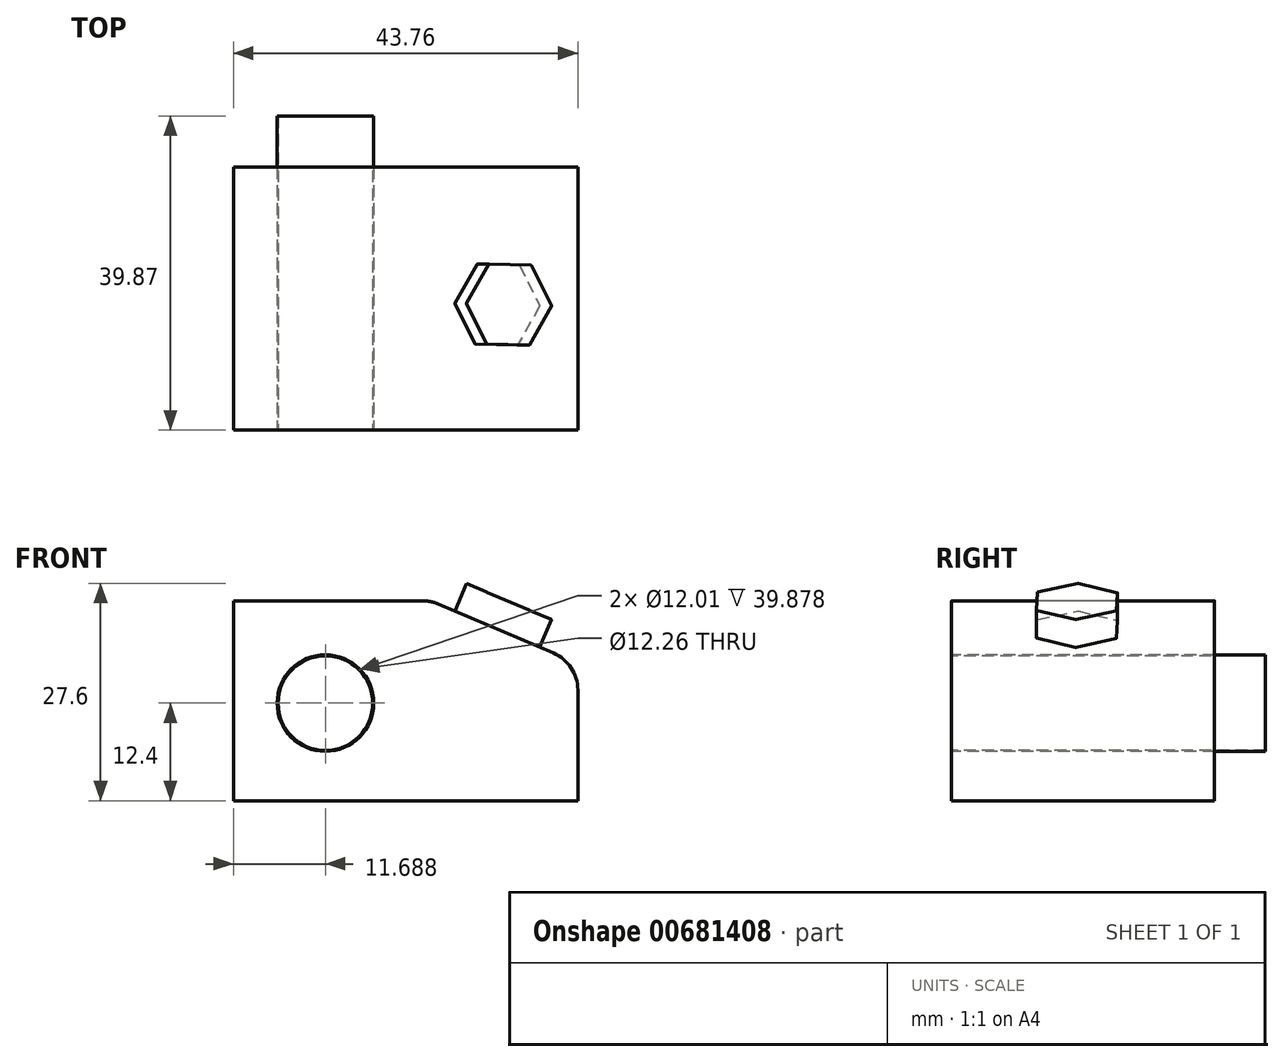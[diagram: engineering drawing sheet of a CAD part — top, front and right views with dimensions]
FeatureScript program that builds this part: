
annotation { "Feature Type Name" : "Feature", "Feature Type Description" : "" }
export const myFeature = defineFeature(function(context is Context, id is Id, definition is map)
    precondition{}
    {
        {
            var Q0;
            Q0=qCreatedBy(makeId("Top.planeOp"),FACE);
            var sketch = newSketch(context, id + "F0", { "sketchPlane" : qUnion([Q0])});
            skLineSegment(sketch, "E0.bottom", {"start": v(-22.53, 17.48) * mm, "end": v(21.23, 17.48) * mm});
            skLineSegment(sketch, "E0.top", {"start": v(-22.53, -15.92) * mm, "end": v(21.23, -15.92) * mm});
            skLineSegment(sketch, "E0.left", {"start": v(-22.53, 17.48) * mm, "end": v(-22.53, -15.92) * mm});
            skLineSegment(sketch, "E0.right", {"start": v(21.23, 17.48) * mm, "end": v(21.23, -15.92) * mm});
            skSolve(sketch);
        }
        {
            var Q0;
            Q0 = qSketchRegion(id + "F0", true);
            extrude(context, id + "F1", {"entities" : qUnion([Q0]), "depth" : 25.4 * mm, "offsetDistance" : 25.4 * mm});
        }
        {
            var Q0;
            Q0=qCreatedBy(makeId("Front.planeOp"),FACE);
            var sketch = newSketch(context, id + "F2", { "sketchPlane" : qUnion([Q0])});
            skLineSegment(sketch, "E1", {"start": v(0, 26.48) * mm, "end": v(22.6, 16.86) * mm});
            skLineSegment(sketch, "E2", {"start": v(22.54, 26.54) * mm, "end": v(0, 26.48) * mm});
            skLineSegment(sketch, "E3", {"start": v(22.6, 16.86) * mm, "end": v(22.54, 26.54) * mm});
            skSolve(sketch);
        }
        {
            var Q0;
            Q0 = qSketchRegion(id + "F2", true);
            extrude(context, id + "F3", {"entities" : qUnion([Q0]), "operationType" : NewBodyOperationType.REMOVE, "oppositeDirection" : true, "depth" : 56.4 * mm, "offsetDistance" : 25.4 * mm, "hasSecondDirection" : true, "secondDirectionOppositeDirection" : false, "secondDirectionDepth" : 25.4 * mm});
        }
        {
            var Q0;
            Q0 = qSketchRegion(id + "F2", true);
            extrude(context, id + "F4", {"entities" : qUnion([Q0]), "operationType" : NewBodyOperationType.REMOVE, "oppositeDirection" : true, "depth" : 25.4 * mm, "offsetDistance" : 25.4 * mm, "hasSecondDirection" : true, "secondDirectionOppositeDirection" : false, "secondDirectionDepth" : 25.4 * mm});
        }
        {
            var Q0;
            Q0=makeQuery(id+"F3.boolean.opBoolean","INTERSECT",EDGE,{"derivedFrom":[makeQuery(id+"F1.opExtrude","CAP_FACE",FACE,{"disambiguationData":[OSD([sQuery(id+"F0.wireOp",EDGE,"E0.bottom"),sQuery(id+"F0.wireOp",EDGE,"E0.top"),sQuery(id+"F0.wireOp",EDGE,"E0.left"),sQuery(id+"F0.wireOp",EDGE,"E0.right")])],"isStart":false}),makeQuery(id+"F3.opExtrude","SWEPT_FACE",FACE,{"disambiguationData":[OSD([sQuery(id+"F2.wireOp",EDGE,"E1")])]})]});
            var Q1;
            Q1=makeQuery(id+"F3.boolean.opBoolean","INTERSECT",EDGE,{"derivedFrom":[makeQuery(id+"F1.opExtrude","SWEPT_FACE",FACE,{"disambiguationData":[OSD([sQuery(id+"F0.wireOp",EDGE,"E0.right")])]}),makeQuery(id+"F3.opExtrude","SWEPT_FACE",FACE,{"disambiguationData":[OSD([sQuery(id+"F2.wireOp",EDGE,"E1")])]})]});
            fillet(context, id + "F5", {"entities" : qUnion([Q0, Q1]), "radius" : 5.08 * mm, "tangentPropagation" : true, "allowEdgeOverflow" : false});
        }
        {
            var Q0;
            Q0=makeQuery(id+"F1.opExtrude","SWEPT_FACE",FACE,{"disambiguationData":[OSD([sQuery(id+"F0.wireOp",EDGE,"E0.top")])]});
            var sketch = newSketch(context, id + "F6", { "sketchPlane" : qUnion([Q0])});
            skCircle(sketch, "E4", {"center": v(-10.84, 12.4) * mm, "radius": 6.13 * mm});
            skSolve(sketch);
        }
        {
            var Q0;
            Q0 = qSketchRegion(id + "F6", true);
            extrude(context, id + "F7", {"entities" : qUnion([Q0]), "operationType" : NewBodyOperationType.REMOVE, "oppositeDirection" : true, "depth" : 50.8 * mm, "offsetDistance" : 25.4 * mm});
        }
        {
            var Q0;
            Q0=makeQuery(id+"F1.opExtrude","SWEPT_FACE",FACE,{"disambiguationData":[OSD([sQuery(id+"F0.wireOp",EDGE,"E0.top")])]});
            var sketch = newSketch(context, id + "F8", { "sketchPlane" : qUnion([Q0])});
            skCircle(sketch, "E5.0", {"center": v(-10.84, 12.4) * mm, "radius": 6.13 * mm});
            skCircle(sketch, "E6", {"center": v(-10.84, 12.4) * mm, "radius": 6 * mm});
            skSolve(sketch);
        }
        {
            var Q0;
            Q0 = qSketchRegion(id + "F8", true);
            extrude(context, id + "F9", {"entities" : qUnion([Q0]), "oppositeDirection" : true, "depth" : 39.88 * mm, "offsetDistance" : 25.4 * mm});
        }
        {
            var Q0;
            Q0=makeQuery(id+"F9.opExtrude","SWEPT_BODY",BODY,{"disambiguationData":[OSD([sQuery(id+"F8.wireOp",EDGE,"E5.0"),sQuery(id+"F8.wireOp",EDGE,"E6")])]});
            transform(context, id + "F10", {"entities" : qUnion([Q0]), "transformType" : TransformType.TRANSLATION_3D, "dx" : 0 * mm, "dy" : 0 * mm, "dz" : 0 * mm, "makeCopy" : true});
        }
        {
            var Q0;
            Q0=makeQuery(id+"F3.boolean.opBoolean","COPY",FACE,{"derivedFrom":makeQuery(id+"F3.opExtrude","SWEPT_FACE",FACE,{"disambiguationData":[OSD([sQuery(id+"F2.wireOp",EDGE,"E1")])]})});
            var sketch = newSketch(context, id + "F11", { "sketchPlane" : qUnion([Q0])});
            skSolve(sketch);
        }
        {
            var Q0;
            {var subQ0=makeQuery(id+"F3.opExtrude","SWEPT_FACE",FACE,{"disambiguationData":[OSD([sQuery(id+"F2.wireOp",EDGE,"E1")])]});var subQ1=sQuery(id+"F0.wireOp",EDGE,"E0.bottom");Q0=makeQuery(id+"F11.imprint","IMPRINT",FACE,{"disambiguationData":[TD([[makeQuery(id+"F11.imprint","IMPRINT",EDGE,{"derivedFrom":makeQuery(id+"F3.boolean.opBoolean","INTERSECT",EDGE,{"derivedFrom":[makeQuery(id+"F1.opExtrude","SWEPT_FACE",FACE,{"disambiguationData":[OSD([subQ1])]}),subQ0]})}),1.0]])]});}
            var sketch = newSketch(context, id + "F12", { "sketchPlane" : qUnion([Q0])});
            skCircle(sketch, "E7.cCircle", {"center": v(1.58, 0) * mm, "radius": 5.08 * mm, "construction": true});
            skLineSegment(sketch, "E7.0", {"start": v(7.44, -0.15) * mm, "end": v(4.38, -5.16) * mm});
            skLineSegment(sketch, "E7.1", {"start": v(4.38, -5.16) * mm, "end": v(-1.49, -5) * mm});
            skLineSegment(sketch, "E7.2", {"start": v(-1.49, -5) * mm, "end": v(-4.29, 0.15) * mm});
            skLineSegment(sketch, "E7.3", {"start": v(-4.29, 0.15) * mm, "end": v(-1.22, 5.16) * mm});
            skLineSegment(sketch, "E7.4", {"start": v(-1.22, 5.16) * mm, "end": v(4.64, 5) * mm});
            skLineSegment(sketch, "E7.5", {"start": v(4.64, 5) * mm, "end": v(7.44, -0.15) * mm});
            skPoint(sketch, "E7.0.midPoint", {"position": v(5.91, -2.65) * mm});
            skSolve(sketch);
        }
        {
            var Q0;
            Q0 = qSketchRegion(id + "F12", true);
            extrude(context, id + "F13", {"entities" : qUnion([Q0]), "operationType" : NewBodyOperationType.ADD, "depth" : 3.8 * mm, "offsetDistance" : 25.4 * mm});
        }
        {
            var Q0;
            Q0=makeQuery(id+"F13.opExtrude","SWEPT_EDGE",EDGE,{"disambiguationData":[OSD([sQuery(id+"F12.wireOp",EDGE,"E7.0"),sQuery(id+"F12.wireOp",EDGE,"E7.1")])]});
            var Q1;
            Q1=makeQuery(id+"F13.opExtrude","SWEPT_EDGE",EDGE,{"disambiguationData":[OSD([sQuery(id+"F12.wireOp",EDGE,"E7.0"),sQuery(id+"F12.wireOp",EDGE,"E7.5")])]});
            var Q2;
            Q2=makeQuery(id+"F13.opExtrude","SWEPT_EDGE",EDGE,{"disambiguationData":[OSD([sQuery(id+"F12.wireOp",EDGE,"E7.4"),sQuery(id+"F12.wireOp",EDGE,"E7.5")])]});
            var Q3;
            Q3=makeQuery(id+"F13.opExtrude","SWEPT_EDGE",EDGE,{"disambiguationData":[OSD([sQuery(id+"F12.wireOp",EDGE,"E7.1"),sQuery(id+"F12.wireOp",EDGE,"E7.2")])]});
            var Q4;
            Q4=makeQuery(id+"F13.opExtrude","SWEPT_EDGE",EDGE,{"disambiguationData":[OSD([sQuery(id+"F12.wireOp",EDGE,"E7.3"),sQuery(id+"F12.wireOp",EDGE,"E7.4")])]});
            var Q5;
            Q5=makeQuery(id+"F13.opExtrude","SWEPT_EDGE",EDGE,{"disambiguationData":[OSD([sQuery(id+"F12.wireOp",EDGE,"E7.2"),sQuery(id+"F12.wireOp",EDGE,"E7.3")])]});
            fillet(context, id + "F14", {"entities" : qUnion([Q0, Q1, Q2, Q3, Q4, Q5]), "radius" : 0.06 * mm, "tangentPropagation" : true, "allowEdgeOverflow" : false});
        }
    });
